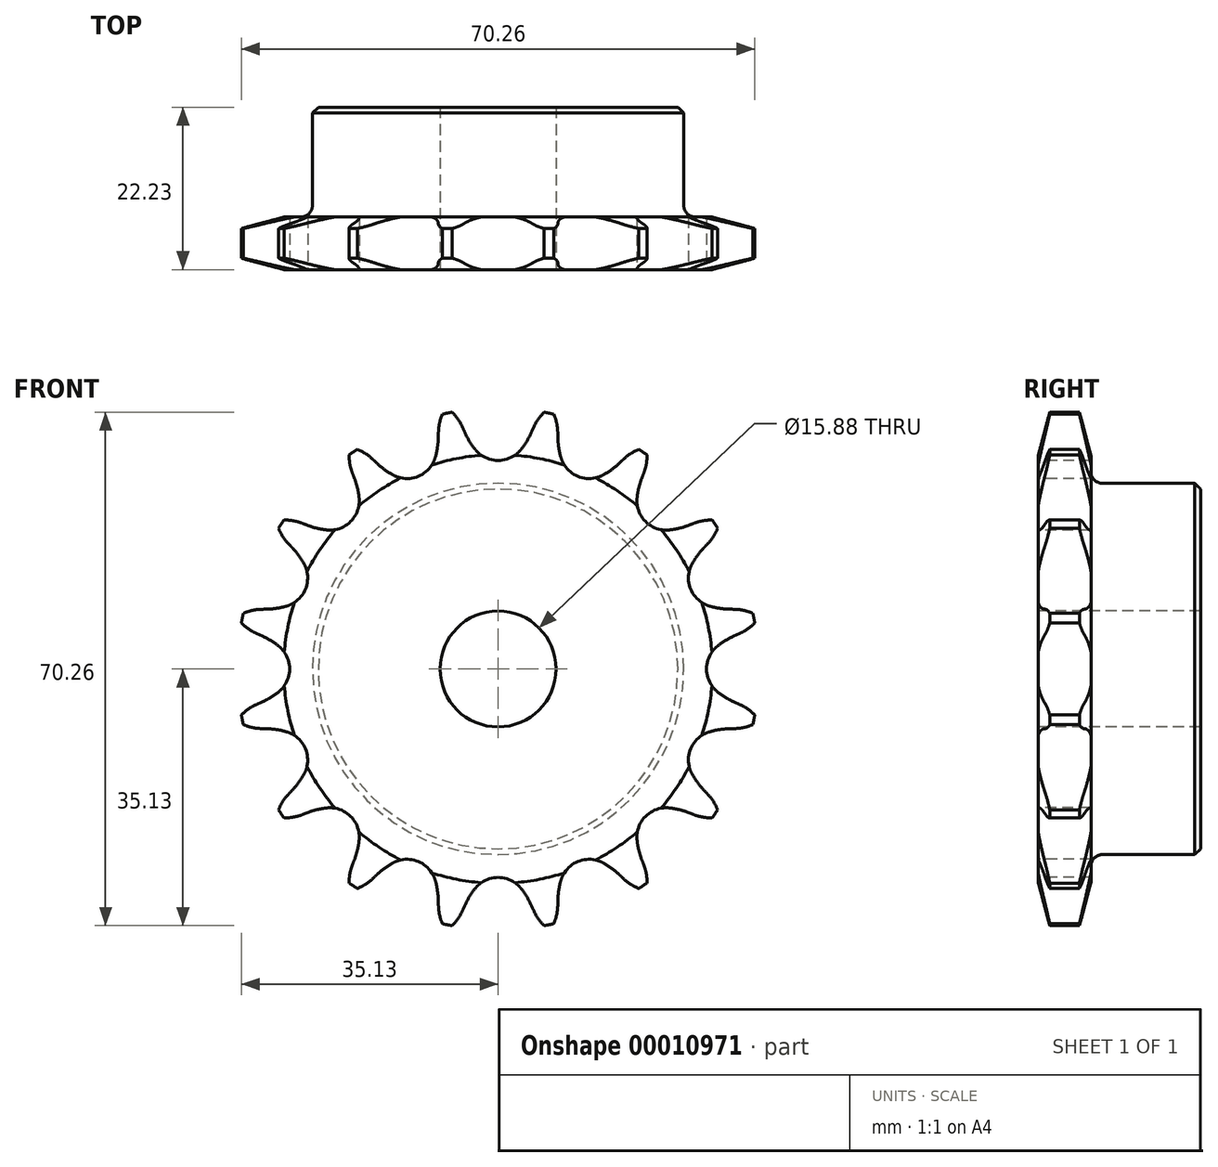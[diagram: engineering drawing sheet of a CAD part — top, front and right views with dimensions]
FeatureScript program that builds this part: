
annotation { "Feature Type Name" : "Feature", "Feature Type Description" : "" }
export const myFeature = defineFeature(function(context is Context, id is Id, definition is map)
    precondition{}
    {
        {
            var Q0;
            Q0=qCreatedBy(makeId("Right.planeOp"),FACE);
            var sketch = newSketch(context, id + "F0", { "sketchPlane" : qUnion([Q0])});
            skLineSegment(sketch, "E0", {"start": v(0, 0) * mm, "end": v(22.22, 0) * mm, "construction": true});
            skLineSegment(sketch, "E1", {"start": v(0, 35.69) * mm, "end": v(7.21, 35.69) * mm});
            skLineSegment(sketch, "E2", {"start": v(7.21, 35.69) * mm, "end": v(7.21, 25.4) * mm});
            skLineSegment(sketch, "E3", {"start": v(7.21, 25.4) * mm, "end": v(22.23, 25.4) * mm});
            skLineSegment(sketch, "E4", {"start": v(22.22, 25.4) * mm, "end": v(22.22, 7.94) * mm});
            skLineSegment(sketch, "E5", {"start": v(22.23, 7.94) * mm, "end": v(0, 7.94) * mm});
            skLineSegment(sketch, "E6", {"start": v(0, 7.94) * mm, "end": v(0, 35.69) * mm});
            skLineSegment(sketch, "E7.0.MirrorCS", {"start": v(0, -35.69) * mm, "end": v(7.21, -35.69) * mm});
            skLineSegment(sketch, "E7.1.MirrorCS", {"start": v(7.21, -35.69) * mm, "end": v(7.21, -25.4) * mm});
            skLineSegment(sketch, "E7.2.MirrorCS", {"start": v(22.23, -7.94) * mm, "end": v(0, -7.94) * mm});
            skLineSegment(sketch, "E7.3.MirrorCS", {"start": v(22.23, -25.4) * mm, "end": v(22.23, -7.94) * mm});
            skLineSegment(sketch, "E7.4.MirrorCS", {"start": v(7.21, -25.4) * mm, "end": v(22.23, -25.4) * mm});
            skLineSegment(sketch, "E7.5.MirrorCS", {"start": v(0, -7.94) * mm, "end": v(0, -35.69) * mm});
            skSolve(sketch);
        }
        {
            var Q0;
            Q0=makeQuery(id+"F0.imprint","IMPRINT",FACE,{"disambiguationData":[TD([[makeQuery(id+"F0.imprint","IMPRINT",EDGE,{"derivedFrom":sQuery(id+"F0.wireOp",EDGE,"E1")}),-1.0]])]});
            var Q1;
            Q1=sQuery(id+"F0.wireOp",EDGE,"E0");
            revolve(context, id + "F1", {"entities" : qUnion([Q0]), "axis" : qUnion([Q1]), "revolveType" : RevolveType.FULL});
        }
        {
            var Q0;
            Q0=makeQuery(id+"F1.opRevolve","SWEPT_EDGE",EDGE,{"disambiguationData":[OSD([sQuery(id+"F0.wireOp",EDGE,"E1"),sQuery(id+"F0.wireOp",EDGE,"E6")])]});
            var Q1;
            Q1=makeQuery(id+"F1.opRevolve","SWEPT_EDGE",EDGE,{"disambiguationData":[OSD([sQuery(id+"F0.wireOp",EDGE,"E1"),sQuery(id+"F0.wireOp",EDGE,"E2")])]});
            chamfer(context, id + "F2", {"entities" : qUnion([Q0, Q1]), "chamferType" : ChamferType.TWO_OFFSETS, "width1" : 6.35 * mm, "oppositeDirection" : false, "width2" : 1.57 * mm, "tangentPropagation" : true});
        }
        {
            var Q0;
            Q0=makeQuery(id+"F1.opRevolve","SWEPT_FACE",FACE,{"disambiguationData":[OSD([sQuery(id+"F0.wireOp",EDGE,"E6")])]});
            var sketch = newSketch(context, id + "F3", { "sketchPlane" : qUnion([Q0])});
            skCircle(sketch, "E8", {"center": v(0, 0) * mm, "radius": 32.55 * mm, "construction": true});
            skLineSegment(sketch, "E9", {"start": v(0, 0) * mm, "end": v(0, 32.55) * mm, "construction": true});
            skLineSegment(sketch, "E10", {"start": v(0, 32.55) * mm, "end": v(25.8, 32.55) * mm, "construction": true});
            skPoint(sketch, "E11", {"position": v(-10.88, 30.38) * mm});
            skPoint(sketch, "E12", {"position": v(4.95, 36.52) * mm});
            skLineSegment(sketch, "E13", {"start": v(0, 32.55) * mm, "end": v(4.95, 36.52) * mm, "construction": true});
            skLineSegment(sketch, "E14", {"start": v(4.95, 36.52) * mm, "end": v(-4.5, 32.26) * mm, "construction": true});
            skLineSegment(sketch, "E15", {"start": v(-4.5, 32.26) * mm, "end": v(-4.88, 33.1) * mm});
            skLineSegment(sketch, "E16", {"start": v(0, 0) * mm, "end": v(-7.12, 35.8) * mm, "construction": true});
            skArc(sketch, "E17", {"start": v(-7.12, 35.8) * mm, "mid": v(-15.95, 26.17) * mm, "end": v(-4.88, 33.1) * mm, "construction": true});
            skArc(sketch, "E18", {"start": v(-4.88, 33.1) * mm, "mid": v(-5.81, 34.6) * mm, "end": v(-7.12, 35.8) * mm});
            skArc(sketch, "E19", {"start": v(-3.14, 30.03) * mm, "mid": v(13.78, 41.93) * mm, "end": v(-4.5, 32.26) * mm, "construction": true});
            skArc(sketch, "E20", {"start": v(-4.5, 32.26) * mm, "mid": v(-3.89, 31.1) * mm, "end": v(-3.14, 30.03) * mm});
            skLineSegment(sketch, "E21", {"start": v(4.4, 12.5) * mm, "end": v(-4.88, 33.1) * mm, "construction": true});
            skArc(sketch, "E22.0.MirrorCS", {"start": v(4.5, 32.26) * mm, "mid": v(3.89, 31.1) * mm, "end": v(3.14, 30.03) * mm});
            skLineSegment(sketch, "E23.0.MirrorCS", {"start": v(4.5, 32.26) * mm, "end": v(4.88, 33.1) * mm});
            skArc(sketch, "E24.0.MirrorCS", {"start": v(4.88, 33.1) * mm, "mid": v(5.81, 34.6) * mm, "end": v(7.12, 35.8) * mm});
            skArc(sketch, "E25", {"start": v(-3.14, 30.03) * mm, "mid": v(0, 28.53) * mm, "end": v(3.14, 30.03) * mm});
            skArc(sketch, "E26", {"start": v(3.14, 30.03) * mm, "mid": v(0, 36.57) * mm, "end": v(-3.14, 30.03) * mm, "construction": true});
            skArc(sketch, "E27.1.0", {"start": v(-17.17, 28.7) * mm, "mid": v(-18.61, 29.74) * mm, "end": v(-20.28, 30.34) * mm});
            skLineSegment(sketch, "E27.1.1", {"start": v(-16.5, 28.08) * mm, "end": v(-17.17, 28.7) * mm});
            skArc(sketch, "E27.1.2", {"start": v(-16.5, 28.08) * mm, "mid": v(-15.5, 27.25) * mm, "end": v(-14.39, 26.55) * mm});
            skArc(sketch, "E27.1.3", {"start": v(-14.39, 26.55) * mm, "mid": v(-10.92, 26.36) * mm, "end": v(-8.6, 28.95) * mm});
            skArc(sketch, "E27.1.4", {"start": v(-8.19, 31.53) * mm, "mid": v(-8.3, 30.22) * mm, "end": v(-8.6, 28.95) * mm});
            skLineSegment(sketch, "E27.1.5", {"start": v(-8.19, 31.53) * mm, "end": v(-8.16, 32.44) * mm});
            skArc(sketch, "E27.1.6", {"start": v(-8.16, 32.44) * mm, "mid": v(-7.87, 34.19) * mm, "end": v(-7.12, 35.8) * mm});
            skArc(sketch, "E27.2.0", {"start": v(-26.85, 19.95) * mm, "mid": v(-28.57, 20.35) * mm, "end": v(-30.34, 20.28) * mm});
            skLineSegment(sketch, "E27.2.1", {"start": v(-26, 19.63) * mm, "end": v(-26.85, 19.95) * mm});
            skArc(sketch, "E27.2.2", {"start": v(-26, 19.63) * mm, "mid": v(-24.74, 19.24) * mm, "end": v(-23.45, 19.02) * mm});
            skArc(sketch, "E27.2.3", {"start": v(-23.45, 19.02) * mm, "mid": v(-20.17, 20.17) * mm, "end": v(-19.02, 23.45) * mm});
            skArc(sketch, "E27.2.4", {"start": v(-19.63, 26) * mm, "mid": v(-19.24, 24.74) * mm, "end": v(-19.02, 23.45) * mm});
            skLineSegment(sketch, "E27.2.5", {"start": v(-19.63, 26) * mm, "end": v(-19.95, 26.85) * mm});
            skArc(sketch, "E27.2.6", {"start": v(-19.95, 26.85) * mm, "mid": v(-20.35, 28.57) * mm, "end": v(-20.28, 30.34) * mm});
            skArc(sketch, "E27.3.0", {"start": v(-32.44, 8.16) * mm, "mid": v(-34.19, 7.87) * mm, "end": v(-35.8, 7.12) * mm});
            skLineSegment(sketch, "E27.3.1", {"start": v(-31.53, 8.19) * mm, "end": v(-32.44, 8.16) * mm});
            skArc(sketch, "E27.3.2", {"start": v(-31.53, 8.19) * mm, "mid": v(-30.22, 8.3) * mm, "end": v(-28.95, 8.6) * mm});
            skArc(sketch, "E27.3.3", {"start": v(-28.95, 8.6) * mm, "mid": v(-26.36, 10.92) * mm, "end": v(-26.55, 14.39) * mm});
            skArc(sketch, "E27.3.4", {"start": v(-28.08, 16.5) * mm, "mid": v(-27.25, 15.5) * mm, "end": v(-26.55, 14.39) * mm});
            skLineSegment(sketch, "E27.3.5", {"start": v(-28.08, 16.5) * mm, "end": v(-28.7, 17.17) * mm});
            skArc(sketch, "E27.3.6", {"start": v(-28.7, 17.17) * mm, "mid": v(-29.74, 18.61) * mm, "end": v(-30.34, 20.28) * mm});
            skArc(sketch, "E27.4.0", {"start": v(-33.1, -4.88) * mm, "mid": v(-34.6, -5.81) * mm, "end": v(-35.8, -7.12) * mm});
            skLineSegment(sketch, "E27.4.1", {"start": v(-32.26, -4.5) * mm, "end": v(-33.1, -4.88) * mm});
            skArc(sketch, "E27.4.2", {"start": v(-32.26, -4.5) * mm, "mid": v(-31.1, -3.89) * mm, "end": v(-30.03, -3.14) * mm});
            skArc(sketch, "E27.4.3", {"start": v(-30.03, -3.14) * mm, "mid": v(-28.53, 0) * mm, "end": v(-30.03, 3.14) * mm});
            skArc(sketch, "E27.4.4", {"start": v(-32.26, 4.5) * mm, "mid": v(-31.1, 3.89) * mm, "end": v(-30.03, 3.14) * mm});
            skLineSegment(sketch, "E27.4.5", {"start": v(-32.26, 4.5) * mm, "end": v(-33.1, 4.88) * mm});
            skArc(sketch, "E27.4.6", {"start": v(-33.1, 4.88) * mm, "mid": v(-34.6, 5.81) * mm, "end": v(-35.8, 7.12) * mm});
            skArc(sketch, "E27.5.0", {"start": v(-28.7, -17.17) * mm, "mid": v(-29.74, -18.61) * mm, "end": v(-30.34, -20.28) * mm});
            skLineSegment(sketch, "E27.5.1", {"start": v(-28.08, -16.5) * mm, "end": v(-28.7, -17.17) * mm});
            skArc(sketch, "E27.5.2", {"start": v(-28.08, -16.5) * mm, "mid": v(-27.25, -15.5) * mm, "end": v(-26.55, -14.39) * mm});
            skArc(sketch, "E27.5.3", {"start": v(-26.55, -14.39) * mm, "mid": v(-26.36, -10.92) * mm, "end": v(-28.95, -8.6) * mm});
            skArc(sketch, "E27.5.4", {"start": v(-31.53, -8.19) * mm, "mid": v(-30.22, -8.3) * mm, "end": v(-28.95, -8.6) * mm});
            skLineSegment(sketch, "E27.5.5", {"start": v(-31.53, -8.19) * mm, "end": v(-32.44, -8.16) * mm});
            skArc(sketch, "E27.5.6", {"start": v(-32.44, -8.16) * mm, "mid": v(-34.19, -7.87) * mm, "end": v(-35.8, -7.12) * mm});
            skArc(sketch, "E27.6.0", {"start": v(-19.95, -26.85) * mm, "mid": v(-20.35, -28.57) * mm, "end": v(-20.28, -30.34) * mm});
            skLineSegment(sketch, "E27.6.1", {"start": v(-19.63, -26) * mm, "end": v(-19.95, -26.85) * mm});
            skArc(sketch, "E27.6.2", {"start": v(-19.63, -26) * mm, "mid": v(-19.24, -24.74) * mm, "end": v(-19.02, -23.45) * mm});
            skArc(sketch, "E27.6.3", {"start": v(-19.02, -23.45) * mm, "mid": v(-20.17, -20.17) * mm, "end": v(-23.45, -19.02) * mm});
            skArc(sketch, "E27.6.4", {"start": v(-26, -19.63) * mm, "mid": v(-24.74, -19.24) * mm, "end": v(-23.45, -19.02) * mm});
            skLineSegment(sketch, "E27.6.5", {"start": v(-26, -19.63) * mm, "end": v(-26.85, -19.95) * mm});
            skArc(sketch, "E27.6.6", {"start": v(-26.85, -19.95) * mm, "mid": v(-28.57, -20.35) * mm, "end": v(-30.34, -20.28) * mm});
            skArc(sketch, "E27.7.0", {"start": v(-8.16, -32.44) * mm, "mid": v(-7.87, -34.19) * mm, "end": v(-7.12, -35.8) * mm});
            skLineSegment(sketch, "E27.7.1", {"start": v(-8.19, -31.53) * mm, "end": v(-8.16, -32.44) * mm});
            skArc(sketch, "E27.7.2", {"start": v(-8.19, -31.53) * mm, "mid": v(-8.3, -30.22) * mm, "end": v(-8.6, -28.95) * mm});
            skArc(sketch, "E27.7.3", {"start": v(-8.6, -28.95) * mm, "mid": v(-10.92, -26.36) * mm, "end": v(-14.39, -26.55) * mm});
            skArc(sketch, "E27.7.4", {"start": v(-16.5, -28.08) * mm, "mid": v(-15.5, -27.25) * mm, "end": v(-14.39, -26.55) * mm});
            skLineSegment(sketch, "E27.7.5", {"start": v(-16.5, -28.08) * mm, "end": v(-17.17, -28.7) * mm});
            skArc(sketch, "E27.7.6", {"start": v(-17.17, -28.7) * mm, "mid": v(-18.61, -29.74) * mm, "end": v(-20.28, -30.34) * mm});
            skArc(sketch, "E27.8.0", {"start": v(4.88, -33.1) * mm, "mid": v(5.81, -34.6) * mm, "end": v(7.12, -35.8) * mm});
            skLineSegment(sketch, "E27.8.1", {"start": v(4.5, -32.26) * mm, "end": v(4.88, -33.1) * mm});
            skArc(sketch, "E27.8.2", {"start": v(4.5, -32.26) * mm, "mid": v(3.89, -31.1) * mm, "end": v(3.14, -30.03) * mm});
            skArc(sketch, "E27.8.3", {"start": v(3.14, -30.03) * mm, "mid": v(0, -28.53) * mm, "end": v(-3.14, -30.03) * mm});
            skArc(sketch, "E27.8.4", {"start": v(-4.5, -32.26) * mm, "mid": v(-3.89, -31.1) * mm, "end": v(-3.14, -30.03) * mm});
            skLineSegment(sketch, "E27.8.5", {"start": v(-4.5, -32.26) * mm, "end": v(-4.88, -33.1) * mm});
            skArc(sketch, "E27.8.6", {"start": v(-4.88, -33.1) * mm, "mid": v(-5.81, -34.6) * mm, "end": v(-7.12, -35.8) * mm});
            skArc(sketch, "E27.9.0", {"start": v(17.17, -28.7) * mm, "mid": v(18.61, -29.74) * mm, "end": v(20.28, -30.34) * mm});
            skLineSegment(sketch, "E27.9.1", {"start": v(16.5, -28.08) * mm, "end": v(17.17, -28.7) * mm});
            skArc(sketch, "E27.9.2", {"start": v(16.5, -28.08) * mm, "mid": v(15.5, -27.25) * mm, "end": v(14.39, -26.55) * mm});
            skArc(sketch, "E27.9.3", {"start": v(14.39, -26.55) * mm, "mid": v(10.92, -26.36) * mm, "end": v(8.6, -28.95) * mm});
            skArc(sketch, "E27.9.4", {"start": v(8.19, -31.53) * mm, "mid": v(8.3, -30.22) * mm, "end": v(8.6, -28.95) * mm});
            skLineSegment(sketch, "E27.9.5", {"start": v(8.19, -31.53) * mm, "end": v(8.16, -32.44) * mm});
            skArc(sketch, "E27.9.6", {"start": v(8.16, -32.44) * mm, "mid": v(7.87, -34.19) * mm, "end": v(7.12, -35.8) * mm});
            skArc(sketch, "E27.10.0", {"start": v(26.85, -19.95) * mm, "mid": v(28.57, -20.35) * mm, "end": v(30.34, -20.28) * mm});
            skLineSegment(sketch, "E27.10.1", {"start": v(26, -19.63) * mm, "end": v(26.85, -19.95) * mm});
            skArc(sketch, "E27.10.2", {"start": v(26, -19.63) * mm, "mid": v(24.74, -19.24) * mm, "end": v(23.45, -19.02) * mm});
            skArc(sketch, "E27.10.3", {"start": v(23.45, -19.02) * mm, "mid": v(20.17, -20.17) * mm, "end": v(19.02, -23.45) * mm});
            skArc(sketch, "E27.10.4", {"start": v(19.63, -26) * mm, "mid": v(19.24, -24.74) * mm, "end": v(19.02, -23.45) * mm});
            skLineSegment(sketch, "E27.10.5", {"start": v(19.63, -26) * mm, "end": v(19.95, -26.85) * mm});
            skArc(sketch, "E27.10.6", {"start": v(19.95, -26.85) * mm, "mid": v(20.35, -28.57) * mm, "end": v(20.28, -30.34) * mm});
            skArc(sketch, "E27.11.0", {"start": v(32.44, -8.16) * mm, "mid": v(34.19, -7.87) * mm, "end": v(35.8, -7.12) * mm});
            skLineSegment(sketch, "E27.11.1", {"start": v(31.53, -8.19) * mm, "end": v(32.44, -8.16) * mm});
            skArc(sketch, "E27.11.2", {"start": v(31.53, -8.19) * mm, "mid": v(30.22, -8.3) * mm, "end": v(28.95, -8.6) * mm});
            skArc(sketch, "E27.11.3", {"start": v(28.95, -8.6) * mm, "mid": v(26.36, -10.92) * mm, "end": v(26.55, -14.39) * mm});
            skArc(sketch, "E27.11.4", {"start": v(28.08, -16.5) * mm, "mid": v(27.25, -15.5) * mm, "end": v(26.55, -14.39) * mm});
            skLineSegment(sketch, "E27.11.5", {"start": v(28.08, -16.5) * mm, "end": v(28.7, -17.17) * mm});
            skArc(sketch, "E27.11.6", {"start": v(28.7, -17.17) * mm, "mid": v(29.74, -18.61) * mm, "end": v(30.34, -20.28) * mm});
            skArc(sketch, "E27.12.0", {"start": v(33.1, 4.88) * mm, "mid": v(34.6, 5.81) * mm, "end": v(35.8, 7.12) * mm});
            skLineSegment(sketch, "E27.12.1", {"start": v(32.26, 4.5) * mm, "end": v(33.1, 4.88) * mm});
            skArc(sketch, "E27.12.2", {"start": v(32.26, 4.5) * mm, "mid": v(31.1, 3.89) * mm, "end": v(30.03, 3.14) * mm});
            skArc(sketch, "E27.12.3", {"start": v(30.03, 3.14) * mm, "mid": v(28.53, 0) * mm, "end": v(30.03, -3.14) * mm});
            skArc(sketch, "E27.12.4", {"start": v(32.26, -4.5) * mm, "mid": v(31.1, -3.89) * mm, "end": v(30.03, -3.14) * mm});
            skLineSegment(sketch, "E27.12.5", {"start": v(32.26, -4.5) * mm, "end": v(33.1, -4.88) * mm});
            skArc(sketch, "E27.12.6", {"start": v(33.1, -4.88) * mm, "mid": v(34.6, -5.81) * mm, "end": v(35.8, -7.12) * mm});
            skArc(sketch, "E27.13.0", {"start": v(28.7, 17.17) * mm, "mid": v(29.74, 18.61) * mm, "end": v(30.34, 20.28) * mm});
            skLineSegment(sketch, "E27.13.1", {"start": v(28.08, 16.5) * mm, "end": v(28.7, 17.17) * mm});
            skArc(sketch, "E27.13.2", {"start": v(28.08, 16.5) * mm, "mid": v(27.25, 15.5) * mm, "end": v(26.55, 14.39) * mm});
            skArc(sketch, "E27.13.3", {"start": v(26.55, 14.39) * mm, "mid": v(26.36, 10.92) * mm, "end": v(28.95, 8.6) * mm});
            skArc(sketch, "E27.13.4", {"start": v(31.53, 8.19) * mm, "mid": v(30.22, 8.3) * mm, "end": v(28.95, 8.6) * mm});
            skLineSegment(sketch, "E27.13.5", {"start": v(31.53, 8.19) * mm, "end": v(32.44, 8.16) * mm});
            skArc(sketch, "E27.13.6", {"start": v(32.44, 8.16) * mm, "mid": v(34.19, 7.87) * mm, "end": v(35.8, 7.12) * mm});
            skArc(sketch, "E27.14.0", {"start": v(19.95, 26.85) * mm, "mid": v(20.35, 28.57) * mm, "end": v(20.28, 30.34) * mm});
            skLineSegment(sketch, "E27.14.1", {"start": v(19.63, 26) * mm, "end": v(19.95, 26.85) * mm});
            skArc(sketch, "E27.14.2", {"start": v(19.63, 26) * mm, "mid": v(19.24, 24.74) * mm, "end": v(19.02, 23.45) * mm});
            skArc(sketch, "E27.14.3", {"start": v(19.02, 23.45) * mm, "mid": v(20.17, 20.17) * mm, "end": v(23.45, 19.02) * mm});
            skArc(sketch, "E27.14.4", {"start": v(26, 19.63) * mm, "mid": v(24.74, 19.24) * mm, "end": v(23.45, 19.02) * mm});
            skLineSegment(sketch, "E27.14.5", {"start": v(26, 19.63) * mm, "end": v(26.85, 19.95) * mm});
            skArc(sketch, "E27.14.6", {"start": v(26.85, 19.95) * mm, "mid": v(28.57, 20.35) * mm, "end": v(30.34, 20.28) * mm});
            skArc(sketch, "E27.15.0", {"start": v(8.16, 32.44) * mm, "mid": v(7.87, 34.19) * mm, "end": v(7.12, 35.8) * mm});
            skLineSegment(sketch, "E27.15.1", {"start": v(8.19, 31.53) * mm, "end": v(8.16, 32.44) * mm});
            skArc(sketch, "E27.15.2", {"start": v(8.19, 31.53) * mm, "mid": v(8.3, 30.22) * mm, "end": v(8.6, 28.95) * mm});
            skArc(sketch, "E27.15.3", {"start": v(8.6, 28.95) * mm, "mid": v(10.92, 26.36) * mm, "end": v(14.39, 26.55) * mm});
            skArc(sketch, "E27.15.4", {"start": v(16.5, 28.08) * mm, "mid": v(15.5, 27.25) * mm, "end": v(14.39, 26.55) * mm});
            skLineSegment(sketch, "E27.15.5", {"start": v(16.5, 28.08) * mm, "end": v(17.17, 28.7) * mm});
            skArc(sketch, "E27.15.6", {"start": v(17.17, 28.7) * mm, "mid": v(18.61, 29.74) * mm, "end": v(20.28, 30.34) * mm});
            skSolve(sketch);
        }
        {
            var Q0;
            Q0=qSketchRegion(id+"F3",true);
            extrude(context, id + "F4", {"entities" : qUnion([Q0]), "operationType" : NewBodyOperationType.INTERSECT, "endBound" : BoundingType.THROUGH_ALL, "oppositeDirection" : true, "depth" : 25.4 * mm});
        }
        {
            var Q0;
            Q0=makeQuery(id+"F1.opRevolve","SWEPT_EDGE",EDGE,{"disambiguationData":[OSD([sQuery(id+"F0.wireOp",EDGE,"E2"),sQuery(id+"F0.wireOp",EDGE,"E3")])]});
            fillet(context, id + "F5", {"entities" : qUnion([Q0]), "radius" : 1.59 * mm, "tangentPropagation" : true, "allowEdgeOverflow" : false});
        }
        {
            var Q0;
            Q0=makeQuery(id+"F1.opRevolve","SWEPT_EDGE",EDGE,{"disambiguationData":[OSD([sQuery(id+"F0.wireOp",EDGE,"E3"),sQuery(id+"F0.wireOp",EDGE,"E4")])]});
            chamfer(context, id + "F6", {"entities" : qUnion([Q0]), "width" : 0.8 * mm, "tangentPropagation" : true});
        }
    });
